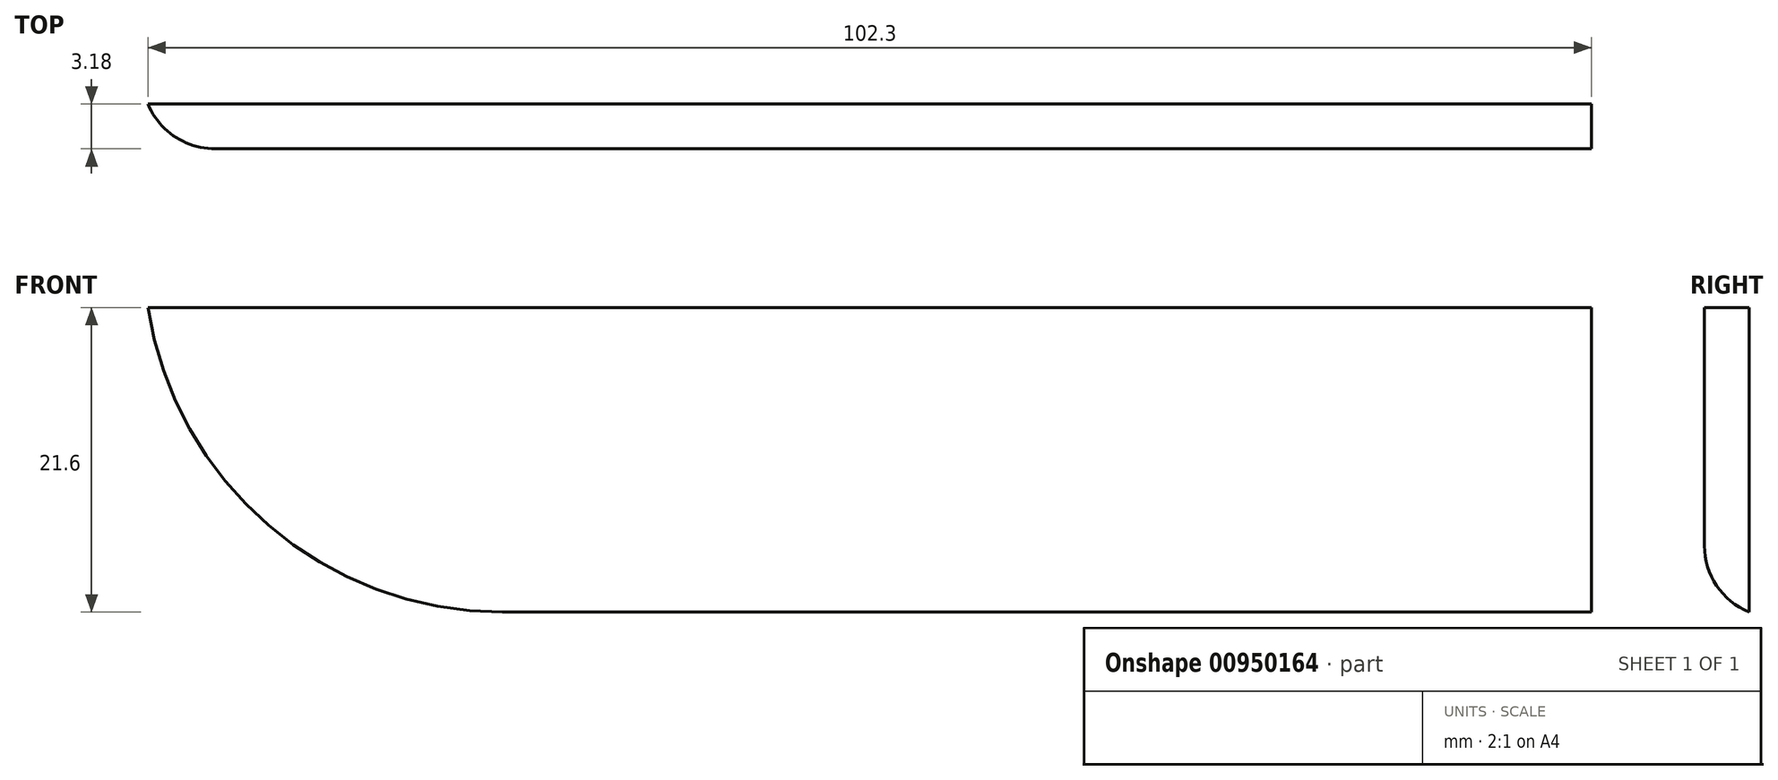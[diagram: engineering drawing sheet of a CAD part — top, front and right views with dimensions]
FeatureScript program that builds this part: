
annotation { "Feature Type Name" : "Feature", "Feature Type Description" : "" }
export const myFeature = defineFeature(function(context is Context, id is Id, definition is map)
    precondition{}
    {
        {
            var Q0;
            Q0=qCreatedBy(makeId("Front.planeOp"),FACE);
            var sketch = newSketch(context, id + "F0", { "sketchPlane" : qUnion([Q0])});
            skLineSegment(sketch, "E0.bottom", {"start": v(51.3, -10.8) * mm, "end": v(-25.9, -10.8) * mm});
            skLineSegment(sketch, "E0.top", {"start": v(51.3, 10.8) * mm, "end": v(-51.3, 10.8) * mm});
            skLineSegment(sketch, "E0.left", {"start": v(51.3, -10.8) * mm, "end": v(51.3, 10.8) * mm});
            skPoint(sketch, "E0.middle", {"position": v(0, 0) * mm});
            skPoint(sketch, "E1.visualSharp", {"position": v(-51.3, -10.8) * mm});
            skArc(sketch, "E1.filletArc", {"start": v(-51, 10.8) * mm, "mid": v(-42.45, -4.66) * mm, "end": v(-25.9, -10.8) * mm});
            skSolve(sketch);
        }
        {
            var Q0;
            Q0=makeQuery(id+"F0.imprint","IMPRINT",FACE,{"disambiguationData":[TD([[makeQuery(id+"F0.imprint","IMPRINT",EDGE,{"derivedFrom":sQuery(id+"F0.wireOp",EDGE,"E0.bottom")}),-1.0]])]});
            extrude(context, id + "F1", {"entities" : qUnion([Q0]), "depth" : 3.17 * mm, "offsetDistance" : 25.4 * mm});
        }
        {
            var Q0;
            Q0=makeQuery(id+"F1.opExtrude","CAP_EDGE",EDGE,{"disambiguationData":[OSD([sQuery(id+"F0.wireOp",EDGE,"E0.bottom")])],"isStart":false});
            fillet(context, id + "F2", {"entities" : qUnion([Q0]), "radius" : 5.08 * mm, "tangentPropagation" : true, "allowEdgeOverflow" : false});
        }
    });
